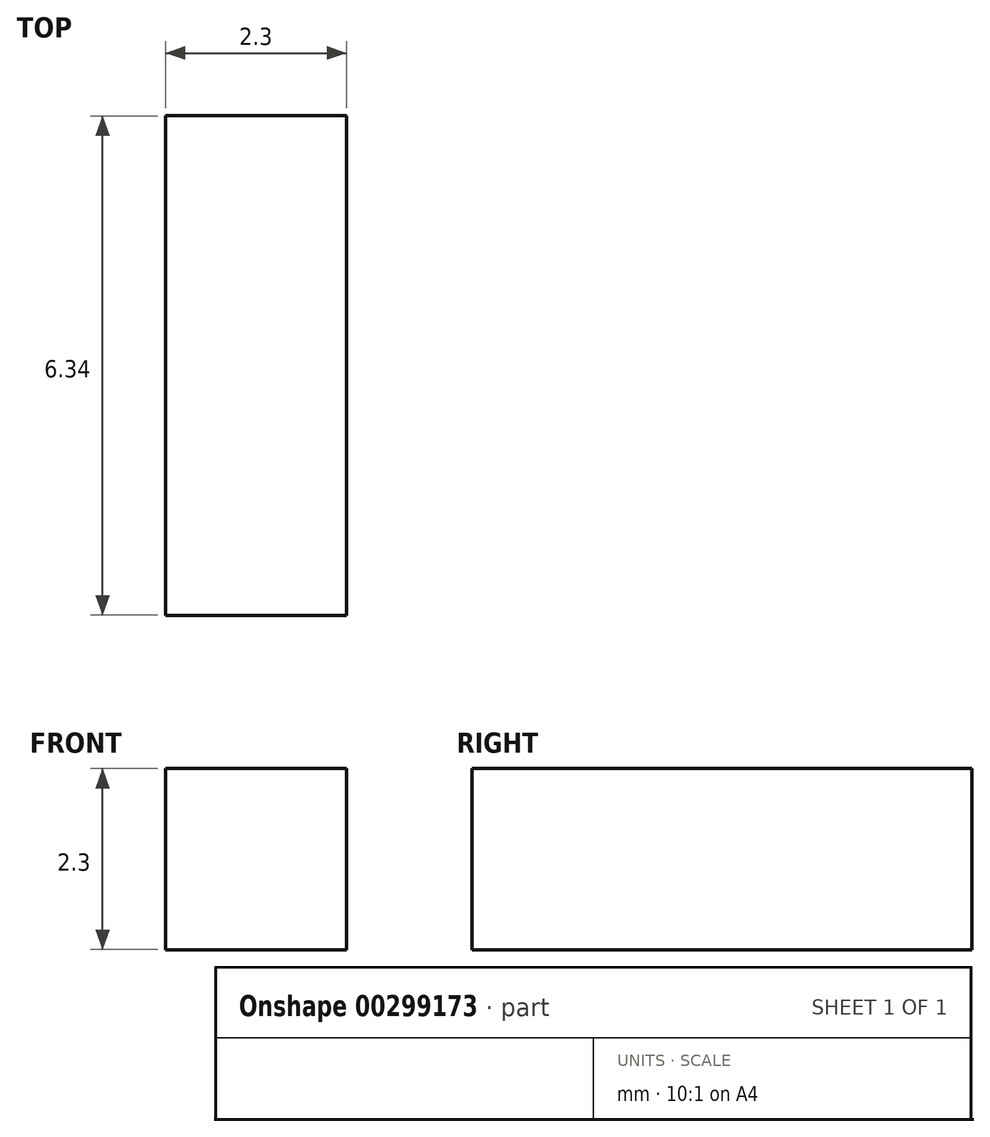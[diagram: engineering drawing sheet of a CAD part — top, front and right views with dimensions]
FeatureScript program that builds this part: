
annotation { "Feature Type Name" : "Feature", "Feature Type Description" : "" }
export const myFeature = defineFeature(function(context is Context, id is Id, definition is map)
    precondition{}
    {
        {
            var Q0;
            Q0=qCreatedBy(makeId("Front.planeOp"),FACE);
            var sketch = newSketch(context, id + "F0", { "sketchPlane" : qUnion([Q0])});
            skLineSegment(sketch, "E0.bottom", {"start": v(1.15, 1.15) * mm, "end": v(-1.15, 1.15) * mm});
            skLineSegment(sketch, "E0.top", {"start": v(1.15, -1.15) * mm, "end": v(-1.15, -1.15) * mm});
            skLineSegment(sketch, "E0.left", {"start": v(1.15, 1.15) * mm, "end": v(1.15, -1.15) * mm});
            skLineSegment(sketch, "E0.right", {"start": v(-1.15, 1.15) * mm, "end": v(-1.15, -1.15) * mm});
            skPoint(sketch, "E0.middle", {"position": v(0, 0) * mm});
            skSolve(sketch);
        }
        {
            var Q0;
            Q0 = qSketchRegion(id + "F0", true);
            extrude(context, id + "F1", {"entities" : qUnion([Q0]), "endBound" : BoundingType.SYMMETRIC, "depth" : 6.35 * mm});
        }
    });
